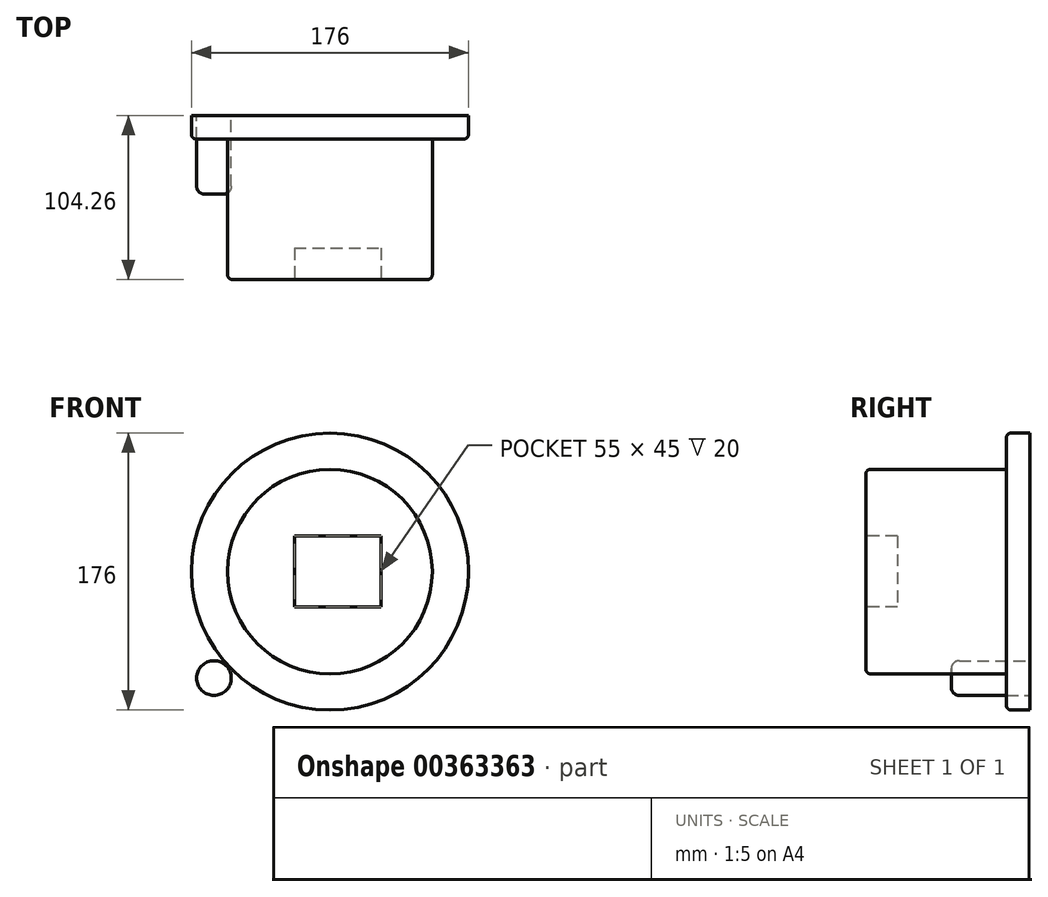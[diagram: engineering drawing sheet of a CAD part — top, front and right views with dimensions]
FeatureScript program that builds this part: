
annotation { "Feature Type Name" : "Feature", "Feature Type Description" : "" }
export const myFeature = defineFeature(function(context is Context, id is Id, definition is map)
    precondition{}
    {
        {
            var Q0;
            Q0=qCreatedBy(makeId("Front.planeOp"),FACE);
            var sketch = newSketch(context, id + "F0", { "sketchPlane" : qUnion([Q0])});
            skCircle(sketch, "E0", {"center": v(23.65, 62.65) * mm, "radius": 65 * mm});
            skCircle(sketch, "E1", {"center": v(-50, -5) * mm, "radius": 11 * mm});
            skCircle(sketch, "E2.0", {"center": v(23.65, 62.65) * mm, "radius": 88 * mm});
            skSolve(sketch);
        }
        {
            var Q0;
            Q0=makeQuery(id+"F0.imprint","IMPRINT",FACE,{"disambiguationData":[TD([[makeQuery(id+"F0.imprint","IMPRINT",EDGE,{"derivedFrom":sQuery(id+"F0.wireOp",EDGE,"E1")}),1.0]])]});
            var Q1;
            Q1=sQuery(id+"F0.wireOp",EDGE,"E1");
            extrude(context, id + "F1", {"entities" : qUnion([Q0]), "surfaceEntities" : qUnion([Q1]), "depth" : 50 * mm});
        }
        {
            var Q0;
            Q0=makeQuery(id+"F0.imprint","IMPRINT",FACE,{"disambiguationData":[TD([[makeQuery(id+"F0.imprint","IMPRINT",EDGE,{"derivedFrom":sQuery(id+"F0.wireOp",EDGE,"E0")}),1.0]])]});
            var Q1;
            Q1=sQuery(id+"F0.wireOp",EDGE,"E0");
            extrude(context, id + "F2", {"entities" : qUnion([Q0]), "surfaceEntities" : qUnion([Q1]), "depth" : 104.26 * mm});
        }
        {
            var Q0;
            Q0=makeQuery(id+"F0.imprint","IMPRINT",FACE,{"disambiguationData":[TD([[makeQuery(id+"F0.imprint","IMPRINT",EDGE,{"derivedFrom":sQuery(id+"F0.wireOp",EDGE,"E0")}),-1.0]])]});
            var Q1;
            Q1=sQuery(id+"F0.wireOp",EDGE,"E2.0");
            extrude(context, id + "F3", {"entities" : qUnion([Q0]), "operationType" : NewBodyOperationType.ADD, "surfaceEntities" : qUnion([Q1]), "depth" : 15 * mm});
        }
        {
            var Q0;
            Q0=makeQuery(id+"F3.opExtrude","CAP_EDGE",EDGE,{"disambiguationData":[OSD([sQuery(id+"F0.wireOp",EDGE,"E2.0")])],"isStart":false});
            var Q1;
            Q1=makeQuery(id+"F2.opExtrude","CAP_EDGE",EDGE,{"disambiguationData":[OSD([sQuery(id+"F0.wireOp",EDGE,"E0")])],"isStart":false});
            fillet(context, id + "F4", {"entities" : qUnion([Q0, Q1]), "radius" : 3 * mm, "tangentPropagation" : true, "allowEdgeOverflow" : false});
        }
        {
            var Q0;
            Q0=makeQuery(id+"F1.opExtrude","CAP_EDGE",EDGE,{"disambiguationData":[OSD([sQuery(id+"F0.wireOp",EDGE,"E1")])],"isStart":false});
            fillet(context, id + "F5", {"entities" : qUnion([Q0]), "radius" : 5 * mm, "tangentPropagation" : true, "allowEdgeOverflow" : false});
        }
        {
            var Q0;
            Q0=makeQuery(id+"F2.opExtrude","CAP_FACE",FACE,{"disambiguationData":[OSD([sQuery(id+"F0.wireOp",EDGE,"E0")])],"isStart":false});
            var sketch = newSketch(context, id + "F6", { "sketchPlane" : qUnion([Q0])});
            skLineSegment(sketch, "E3.bottom", {"start": v(1.15, 85.15) * mm, "end": v(56.15, 85.15) * mm});
            skLineSegment(sketch, "E3.top", {"start": v(1.15, 40.15) * mm, "end": v(56.15, 40.15) * mm});
            skLineSegment(sketch, "E3.left", {"start": v(1.15, 85.15) * mm, "end": v(1.15, 40.15) * mm});
            skLineSegment(sketch, "E3.right", {"start": v(56.15, 85.15) * mm, "end": v(56.15, 40.15) * mm});
            skSolve(sketch);
        }
        {
            var Q0;
            Q0 = qSketchRegion(id + "F6", true);
            extrude(context, id + "F7", {"entities" : qUnion([Q0]), "operationType" : NewBodyOperationType.REMOVE, "oppositeDirection" : true, "depth" : 20 * mm});
        }
    });
